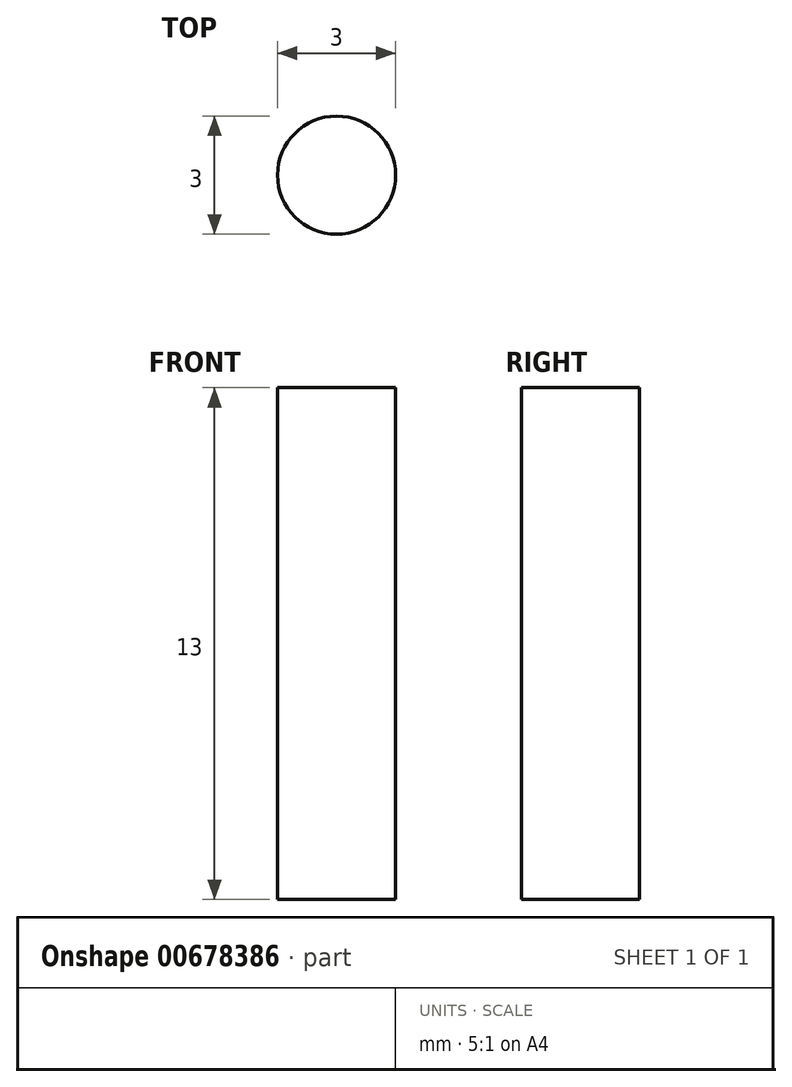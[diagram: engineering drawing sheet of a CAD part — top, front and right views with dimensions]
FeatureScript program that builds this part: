
annotation { "Feature Type Name" : "Feature", "Feature Type Description" : "" }
export const myFeature = defineFeature(function(context is Context, id is Id, definition is map)
    precondition{}
    {
        {
            var Q0;
            Q0=qCreatedBy(makeId("Top.planeOp"),FACE);
            var sketch = newSketch(context, id + "F0", { "sketchPlane" : qUnion([Q0])});
            skCircle(sketch, "E0", {"center": v(0, 0) * mm, "radius": 1.5 * mm});
            skSolve(sketch);
        }
        {
            var Q0;
            Q0 = qSketchRegion(id + "F0", true);
            extrude(context, id + "F1", {"entities" : qUnion([Q0]), "depth" : 13 * mm, "offsetDistance" : 25 * mm});
        }
    });
